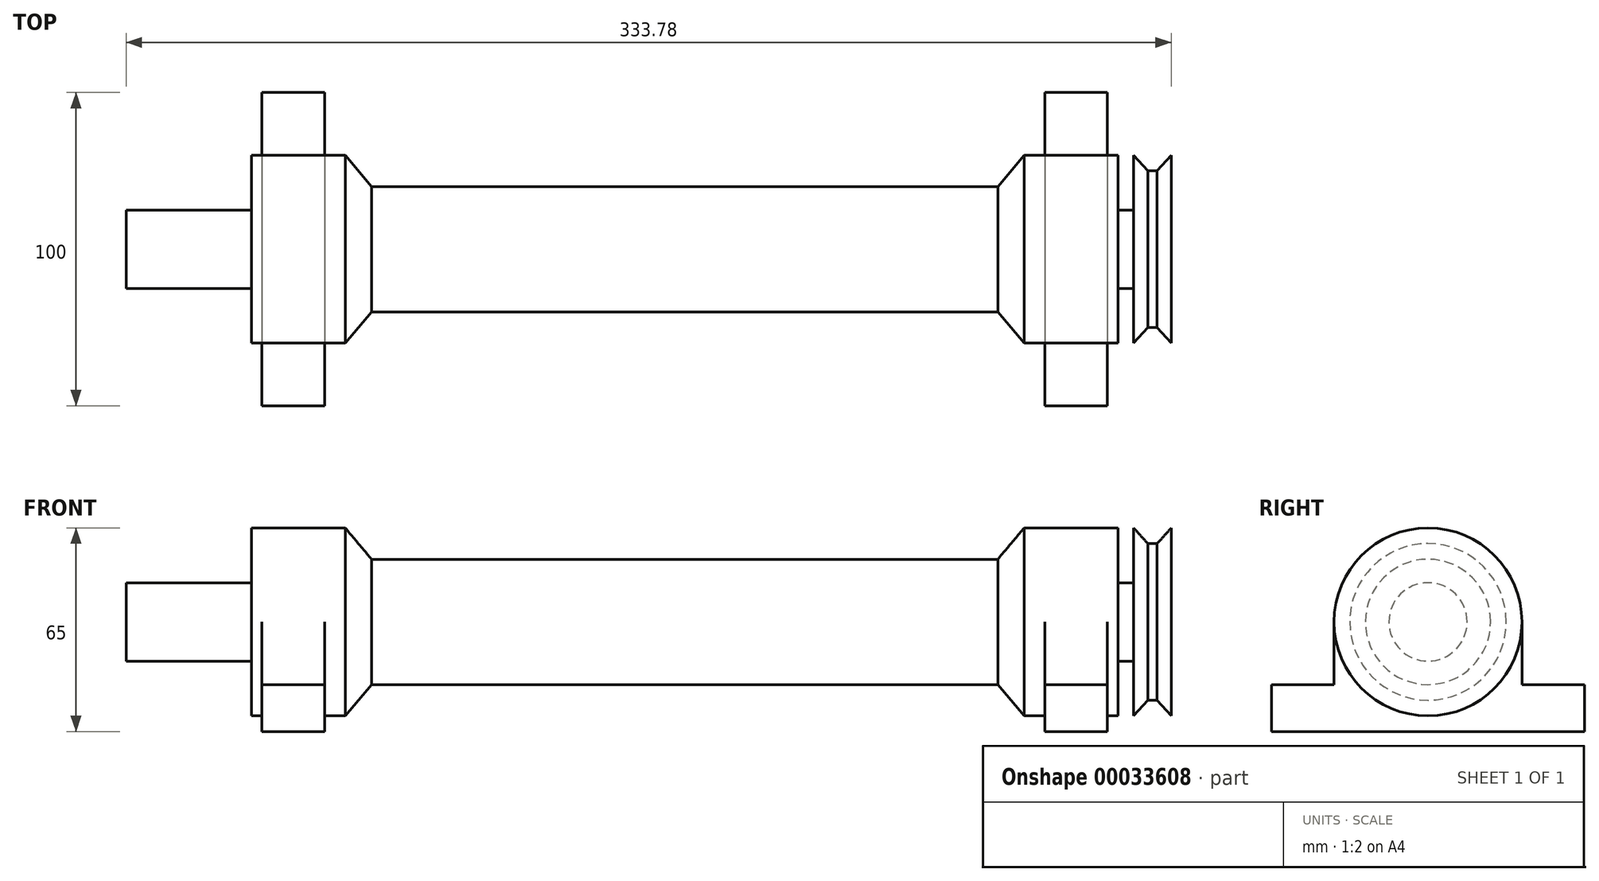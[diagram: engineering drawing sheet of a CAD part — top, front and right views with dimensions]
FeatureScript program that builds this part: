
annotation { "Feature Type Name" : "Feature", "Feature Type Description" : "" }
export const myFeature = defineFeature(function(context is Context, id is Id, definition is map)
    precondition{}
    {
        {
            var Q0;
            Q0=qCreatedBy(makeId("Front.planeOp"),FACE);
            var sketch = newSketch(context, id + "F0", { "sketchPlane" : qUnion([Q0])});
            skLineSegment(sketch, "E0", {"start": v(-138.4, 30) * mm, "end": v(-108.4, 30) * mm});
            skLineSegment(sketch, "E1", {"start": v(-108.4, 30) * mm, "end": v(-100, 20) * mm});
            skLineSegment(sketch, "E2", {"start": v(-100, 20) * mm, "end": v(100, 20) * mm});
            skLineSegment(sketch, "E3", {"start": v(100, 20) * mm, "end": v(108.4, 30) * mm});
            skLineSegment(sketch, "E4", {"start": v(108.4, 30) * mm, "end": v(138.4, 30) * mm});
            skLineSegment(sketch, "E5", {"start": v(138.4, 30) * mm, "end": v(138.4, 12.5) * mm});
            skLineSegment(sketch, "E6", {"start": v(138.4, 12.5) * mm, "end": v(143.4, 12.5) * mm});
            skLineSegment(sketch, "E7", {"start": v(143.4, 12.5) * mm, "end": v(143.4, 30) * mm});
            skLineSegment(sketch, "E8", {"start": v(143.4, 30) * mm, "end": v(147.9, 25) * mm});
            skLineSegment(sketch, "E9", {"start": v(147.9, 25) * mm, "end": v(150.9, 25) * mm});
            skLineSegment(sketch, "E10", {"start": v(150.9, 25) * mm, "end": v(155.4, 30) * mm});
            skLineSegment(sketch, "E11", {"start": v(155.4, 30) * mm, "end": v(155.4, 0) * mm});
            skLineSegment(sketch, "E12", {"start": v(155.4, 0) * mm, "end": v(-178.4, 0) * mm});
            skLineSegment(sketch, "E13", {"start": v(-178.4, 0) * mm, "end": v(-178.4, 12.5) * mm});
            skLineSegment(sketch, "E14", {"start": v(-178.4, 12.5) * mm, "end": v(-138.4, 12.5) * mm});
            skLineSegment(sketch, "E15", {"start": v(-138.4, 12.5) * mm, "end": v(-138.4, 30) * mm});
            skPoint(sketch, "E16", {"position": v(0, 20) * mm});
            skPoint(sketch, "E17", {"position": v(149.4, 25) * mm});
            skPoint(sketch, "E18", {"position": v(95.98, 24.28) * mm});
            skLineSegment(sketch, "E19", {"start": v(149.4, 25) * mm, "end": v(149.4, 27.88) * mm, "construction": true});
            skLineSegment(sketch, "E20", {"start": v(-156.38, 0) * mm, "end": v(148.64, 0) * mm, "construction": true});
            skPoint(sketch, "E20.startSnap0", {"position": v(-11.5, 0) * mm});
            skSolve(sketch);
        }
        {
            var Q0;
            Q0 = qSketchRegion(id + "F0", true);
            var Q1;
            Q1=makeQuery(id+"F0.imprint","IMPRINT",FACE,{"disambiguationData":[TD([[makeQuery(id+"F0.imprint","IMPRINT",EDGE,{"derivedFrom":sQuery(id+"F0.wireOp",EDGE,"E0")}),-1.0]])]});
            var Q2;
            Q2=sQuery(id+"F0.wireOp",EDGE,"E20");
            revolve(context, id + "F1", {"entities" : qUnion([Q0, Q1]), "axis" : qUnion([Q2]), "revolveType" : RevolveType.FULL});
        }
        {
            var Q0;
            Q0=qCreatedBy(makeId("Top.planeOp"),FACE);
            var sketch = newSketch(context, id + "F2", { "sketchPlane" : qUnion([Q0])});
            skLineSegment(sketch, "E21.bottom", {"start": v(-135, 50) * mm, "end": v(-115, 50) * mm});
            skLineSegment(sketch, "E21.top", {"start": v(-135, -50) * mm, "end": v(-115, -50) * mm});
            skLineSegment(sketch, "E21.left", {"start": v(-135, 50) * mm, "end": v(-135, -50) * mm});
            skLineSegment(sketch, "E21.right", {"start": v(-115, 50) * mm, "end": v(-115, -50) * mm});
            skPoint(sketch, "E22", {"position": v(-115, 0) * mm});
            skLineSegment(sketch, "E23.bottom", {"start": v(115, 50) * mm, "end": v(135, 50) * mm});
            skLineSegment(sketch, "E23.top", {"start": v(115, -50) * mm, "end": v(135, -50) * mm});
            skLineSegment(sketch, "E23.left", {"start": v(115, 50) * mm, "end": v(115, -50) * mm});
            skLineSegment(sketch, "E23.right", {"start": v(135, 50) * mm, "end": v(135, -50) * mm});
            skSolve(sketch);
        }
        {
            var Q0;
            Q0 = qSketchRegion(id + "F2", true);
            extrude(context, id + "F3", {"entities" : qUnion([Q0]), "operationType" : NewBodyOperationType.ADD, "oppositeDirection" : true, "depth" : 35 * mm});
        }
        {
            var Q0;
            {var subQ0=sQuery(id+"F2.wireOp",EDGE,"E23.bottom");var subQ1=sQuery(id+"F2.wireOp",EDGE,"E23.left");var subQ2=sQuery(id+"F2.wireOp",EDGE,"E23.right");Q0=makeQuery(id+"F3.boolean.opBoolean","SPLIT",FACE,{"disambiguationData":[TD([makeQuery(id+"F3.opExtrude","SWEPT_FACE",FACE,{"disambiguationData":[OSD([subQ0])]})])],"derivedFrom":makeQuery(id+"F3.opExtrude","CAP_FACE",FACE,{"disambiguationData":[OSD([subQ0,sQuery(id+"F2.wireOp",EDGE,"E23.top"),subQ1,subQ2])],"isStart":true})});}
            var sketch = newSketch(context, id + "F4", { "sketchPlane" : qUnion([Q0])});
            skLineSegment(sketch, "E24.0", {"start": v(-135, 50) * mm, "end": v(-135, 30) * mm});
            skLineSegment(sketch, "E25.0", {"start": v(-135, 30) * mm, "end": v(-115, 30) * mm});
            skLineSegment(sketch, "E26.0", {"start": v(-115, 50) * mm, "end": v(-115, 30) * mm});
            skLineSegment(sketch, "E27.0", {"start": v(-135, 50) * mm, "end": v(-115, 50) * mm});
            skLineSegment(sketch, "E28.0", {"start": v(-115, -30) * mm, "end": v(-115, -50) * mm});
            skLineSegment(sketch, "E29.0", {"start": v(-135, -50) * mm, "end": v(-115, -50) * mm});
            skLineSegment(sketch, "E30.0", {"start": v(-135, -30) * mm, "end": v(-135, -50) * mm});
            skLineSegment(sketch, "E31.0", {"start": v(-115, -30) * mm, "end": v(-135, -30) * mm});
            skLineSegment(sketch, "E32.0", {"start": v(115, -30) * mm, "end": v(115, -50) * mm});
            skLineSegment(sketch, "E33.0", {"start": v(115, -50) * mm, "end": v(135, -50) * mm});
            skLineSegment(sketch, "E34.0", {"start": v(135, -30) * mm, "end": v(135, -50) * mm});
            skLineSegment(sketch, "E35.0", {"start": v(135, -30) * mm, "end": v(115, -30) * mm});
            skLineSegment(sketch, "E36.0", {"start": v(115, 50) * mm, "end": v(135, 50) * mm});
            skLineSegment(sketch, "E37.0", {"start": v(135, 50) * mm, "end": v(135, 30) * mm});
            skLineSegment(sketch, "E38.0", {"start": v(115, 30) * mm, "end": v(135, 30) * mm});
            skLineSegment(sketch, "E39.0", {"start": v(115, 50) * mm, "end": v(115, 30) * mm});
            skSolve(sketch);
        }
        {
            var Q0;
            Q0 = qSketchRegion(id + "F4", true);
            extrude(context, id + "F5", {"entities" : qUnion([Q0]), "operationType" : NewBodyOperationType.REMOVE, "oppositeDirection" : true, "depth" : 20 * mm});
        }
    });
